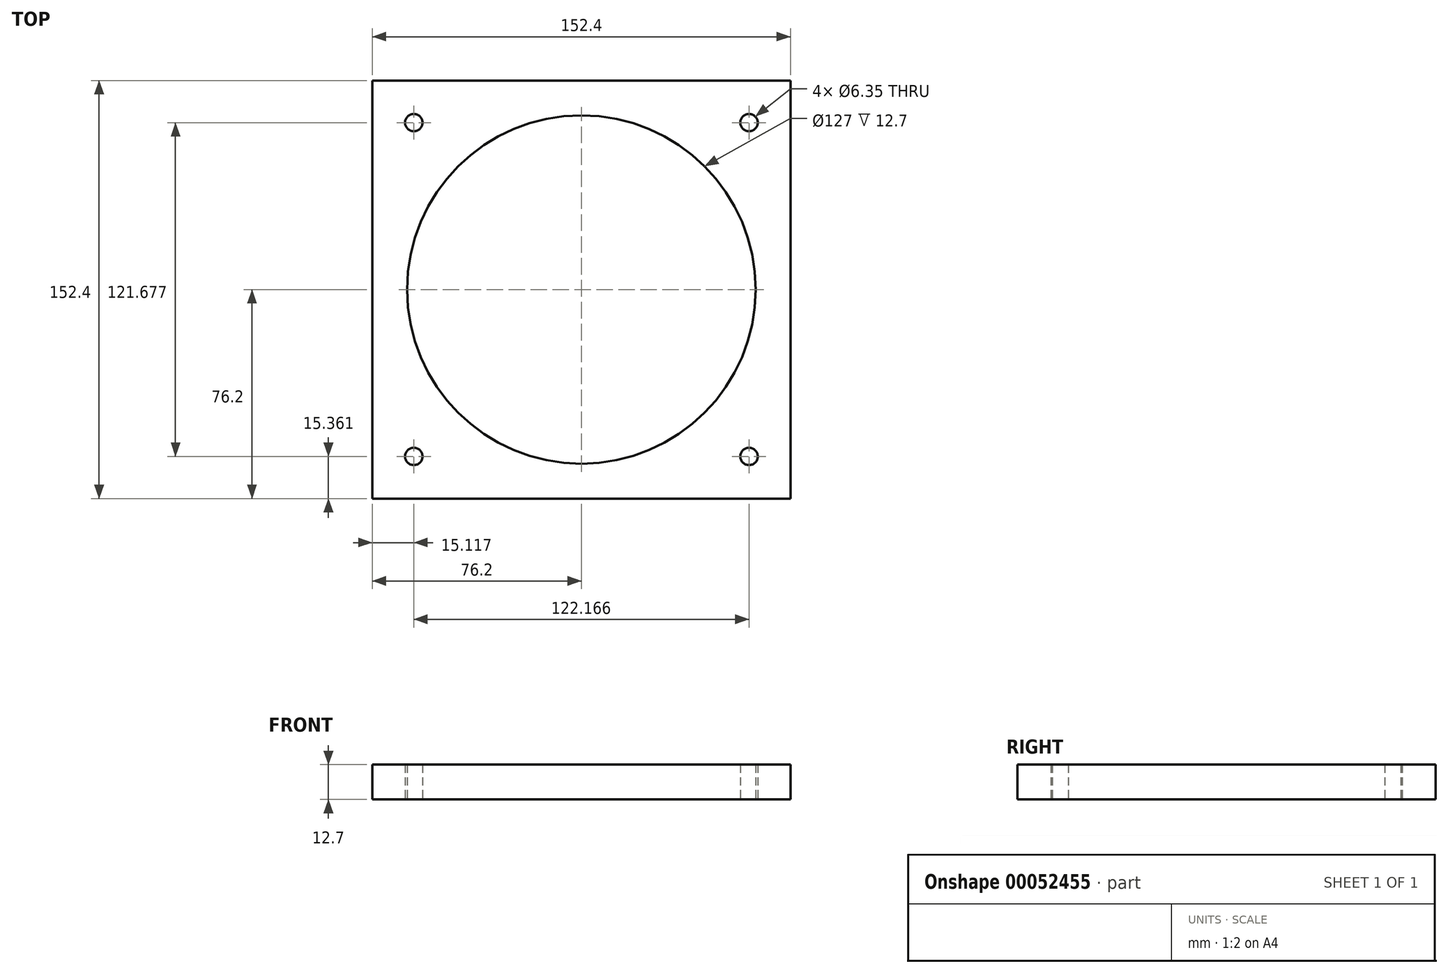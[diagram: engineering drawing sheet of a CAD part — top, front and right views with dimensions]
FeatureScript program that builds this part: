
annotation { "Feature Type Name" : "Feature", "Feature Type Description" : "" }
export const myFeature = defineFeature(function(context is Context, id is Id, definition is map)
    precondition{}
    {
        {
            var Q0;
            Q0=qCreatedBy(makeId("Top.planeOp"),FACE);
            var sketch = newSketch(context, id + "F0", { "sketchPlane" : qUnion([Q0])});
            skCircle(sketch, "E0", {"center": v(0, 0) * mm, "radius": 63.5 * mm});
            skLineSegment(sketch, "E1.rect.bottom", {"start": v(76.2, -76.2) * mm, "end": v(-76.2, -76.2) * mm});
            skLineSegment(sketch, "E1.rect.top", {"start": v(76.2, 76.2) * mm, "end": v(-76.2, 76.2) * mm});
            skLineSegment(sketch, "E1.rect.left", {"start": v(76.2, -76.2) * mm, "end": v(76.2, 76.2) * mm});
            skLineSegment(sketch, "E1.rect.right", {"start": v(-76.2, -76.2) * mm, "end": v(-76.2, 76.2) * mm});
            skCircle(sketch, "E2", {"center": v(-61.08, 60.84) * mm, "radius": 3.18 * mm});
            skCircle(sketch, "E3", {"center": v(61.08, 60.84) * mm, "radius": 3.18 * mm});
            skCircle(sketch, "E4", {"center": v(61.08, -60.84) * mm, "radius": 3.18 * mm});
            skCircle(sketch, "E5", {"center": v(-61.08, -60.84) * mm, "radius": 3.18 * mm});
            skSolve(sketch);
        }
        {
            var Q0;
            Q0=makeQuery(id+"F0.imprint","IMPRINT",FACE,{"disambiguationData":[TD([[makeQuery(id+"F0.imprint","IMPRINT",EDGE,{"derivedFrom":sQuery(id+"F0.wireOp",EDGE,"E0")}),-1.0]])]});
            extrude(context, id + "F1", {"entities" : qUnion([Q0]), "depth" : 12.7 * mm});
        }
    });
